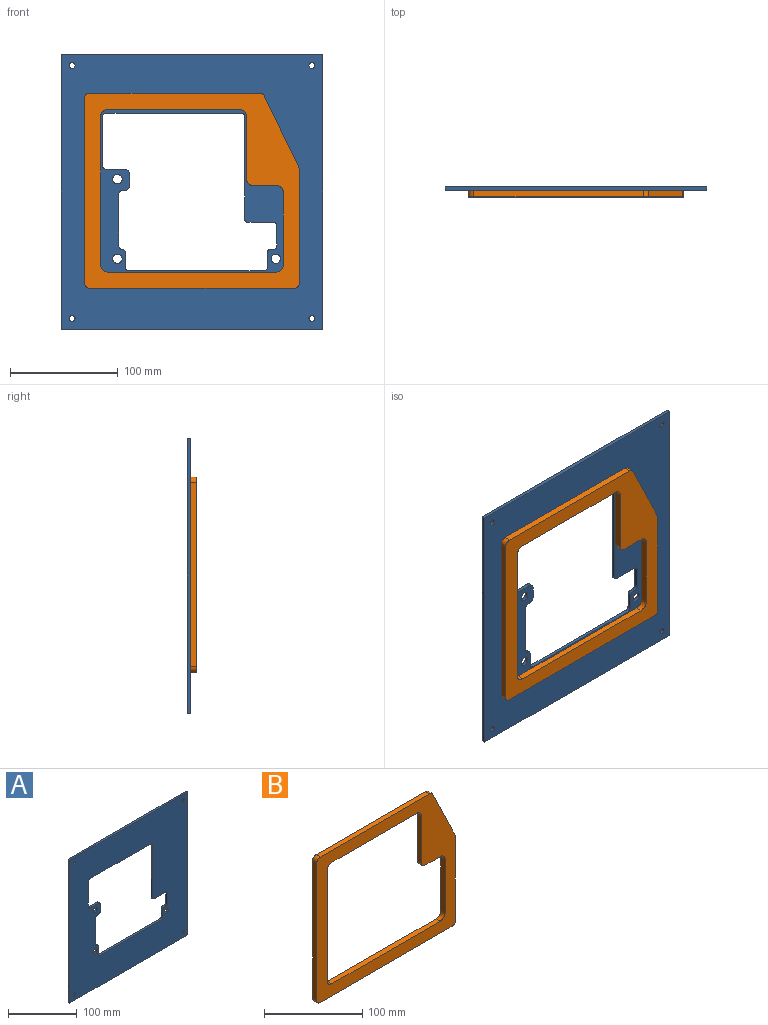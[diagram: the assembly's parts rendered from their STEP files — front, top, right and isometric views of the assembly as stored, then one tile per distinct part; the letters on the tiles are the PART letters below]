
ASSEMBLY  parts=2 mates=1
PART A: 40 faces, bbox 243x3.2x255 mm
  f0: plane 243x3.18mm, normal (0,0,-1), area 771.5mm2, adj f2,f3,f34,f35
  f1: plane 243x3.18mm, normal (0,0,1), area 771.5mm2, adj f2,f3,f34,f35
  f2: plane 255x243mm, normal (0,-1,0), area 42919.9mm2, adj f0,f1,f4,f5,f6,f7,f8,f9
  f3: plane 255x243mm, normal (0,1,0), area 42919.9mm2, adj f0,f1,f4,f5,f6,f7,f8,f9
  f4: plane 95.5x3.18mm, normal (-1,0,0), area 303.2mm2, adj f2,f3,f17,f22
  f5: plane 126x3.18mm, normal (0,0,-1), area 400.1mm2, adj f2,f3,f17,f18
  f6: plane 46x3.18mm, normal (1,0,0), area 146.1mm2, adj f2,f3,f18,f19
  f7: plane 17x3.18mm, normal (0,0,1), area 54mm2, adj f2,f3,f19,f29
  f8: plane 10x3.18mm, normal (1,0,0), area 31.8mm2, adj f2,f3,f29,f30
  f9: plane 3.18x2mm, normal (0,0,-1), area 6.4mm2, adj f2,f3,f23,f30
  f10: plane 48.5x3.18mm, normal (1,0,0), area 154mm2, adj f2,f3,f23,f25
  f11: plane 14x3.18mm, normal (1,0,0), area 44.5mm2, adj f2,f3,f24,f26
  f12: plane 126x3.18mm, normal (0,0,1), area 400.1mm2, adj f2,f3,f20,f26
  f13: plane 14x3.18mm, normal (-1,0,0), area 44.5mm2, adj f2,f3,f20,f21
  f14: plane 3.18x3mm, normal (0,0,1), area 9.5mm2, adj f2,f3,f21,f27
  f15: plane 19x3.18mm, normal (-1,0,0), area 60.3mm2, adj f2,f3,f27,f28
  f16: plane 24x3.18mm, normal (0,0,-1), area 76.2mm2, adj f2,f3,f22,f28
  f17: cylinder r=3mm len=3.18mm, axis (0,-1,0), area 15mm2, adj f2,f3,f4,f5
  f18: cylinder r=3mm len=3.18mm, axis (0,-1,0), area 15mm2, adj f2,f3,f5,f6
  f19: cylinder r=3mm len=3.18mm, axis (0,-1,0), area 15mm2, adj f2,f3,f6,f7
  f20: cylinder r=3mm len=3.18mm, axis (0,-1,0), area 15mm2, adj f2,f3,f12,f13
  f21: cylinder r=3mm len=3.18mm, axis (0,-1,0), area 15mm2, adj f2,f3,f13,f14
  f22: cylinder r=3mm len=3.18mm, axis (0,-1,0), area 15mm2, adj f2,f3,f4,f16
  f23: cylinder r=3mm len=3.18mm, axis (0,-1,0), area 15mm2, adj f2,f3,f9,f10
  f24: cylinder r=3mm len=3.18mm, axis (0,1,0), area 15mm2, adj f2,f3,f11,f25
  f25: cylinder r=3mm len=3.18mm, axis (0,1,0), area 15mm2, adj f2,f3,f10,f24
  f26: cylinder r=3mm len=3.18mm, axis (0,1,0), area 15mm2, adj f2,f3,f11,f12
  f27: cylinder r=3mm len=3.18mm, axis (0,1,0), area 15mm2, adj f2,f3,f14,f15
  f28: cylinder r=3mm len=3.18mm, axis (0,-1,0), area 15mm2, adj f2,f3,f15,f16
  f29: cylinder r=5mm len=5mm, axis (0,-1,0), area 24.9mm2, adj f2,f3,f7,f8
  f30: cylinder r=5mm len=5mm, axis (0,1,0), area 24.9mm2, adj f2,f3,f8,f9
  f31: cylinder r=4.38mm len=8.75mm, axis (0,-1,0), area 87.3mm2, adj f2,f3
  f32: cylinder r=4.38mm len=8.75mm, axis (0,-1,0), area 87.3mm2, adj f2,f3
  f33: cylinder r=4.38mm len=8.75mm, axis (0,-1,0), area 87.3mm2, adj f2,f3
  f34: plane 255x3.18mm, normal (-1,0,0), area 809.6mm2, adj f0,f1,f2,f3
  f35: plane 255x3.18mm, normal (1,0,0), area 809.6mm2, adj f0,f1,f2,f3
  f36: cylinder r=2.75mm len=5.5mm, axis (0,-1,0), area 54.9mm2, adj f2,f3
  f37: cylinder r=2.75mm len=5.5mm, axis (0,-1,0), area 54.9mm2, adj f2,f3
  f38: cylinder r=2.75mm len=5.5mm, axis (0,-1,0), area 54.9mm2, adj f2,f3
  f39: cylinder r=2.75mm len=5.5mm, axis (0,-1,0), area 54.9mm2, adj f2,f3
PART B: 24 faces, bbox 200x6x181.5 mm
  f0: plane 200x181.5mm, normal (0,-1,0), area 11777.1mm2, adj f2,f3,f4,f5,f6,f7,f8,f9
  f1: plane 200x181.5mm, normal (0,1,0), area 11777.1mm2, adj f2,f3,f4,f5,f6,f7,f8,f9
  f2: plane 156x6mm, normal (0,0,1), area 936mm2, adj f0,f1,f8,f12
  f3: plane 66.75x6mm, normal (-1,0,0), area 400.5mm2, adj f0,f1,f8,f9
  f4: plane 22x6mm, normal (0,0,-1), area 132mm2, adj f0,f1,f9,f13
  f5: plane 58.75x6mm, normal (-1,0,0), area 352.5mm2, adj f0,f1,f10,f13
  f6: plane 122x6mm, normal (0,0,-1), area 732mm2, adj f0,f1,f10,f11
  f7: plane 137.5x6mm, normal (1,0,0), area 825mm2, adj f0,f1,f11,f12
  f8: cylinder r=7mm len=7mm, axis (0,-1,0), area 66mm2, adj f0,f1,f2,f3
  f9: cylinder r=7mm len=7mm, axis (0,1,0), area 66mm2, adj f0,f1,f3,f4
  f10: cylinder r=7mm len=7mm, axis (0,-1,0), area 66mm2, adj f0,f1,f5,f6
  f11: cylinder r=7mm len=7mm, axis (0,-1,0), area 66mm2, adj f0,f1,f6,f7
  f12: cylinder r=7mm len=7mm, axis (0,1,0), area 66mm2, adj f0,f1,f2,f7
  f13: cylinder r=5mm len=6mm, axis (0,1,0), area 47.1mm2, adj f0,f1,f4,f5
  f14: plane 190x6mm, normal (0,0,-1), area 1140mm2, adj f0,f1,f19,f23
  f15: plane 171.5x6mm, normal (-1,0,0), area 1029mm2, adj f0,f1,f19,f20
  f16: plane 157.86x6mm, normal (0,0,1), area 947.1mm2, adj f0,f1,f20,f21
  f17: plane 66.89x32.14mm, normal (0.9,0,0.43), area 445.3mm2, adj f0,f1,f21,f22
  f18: plane 104.61x6mm, normal (1,0,0), area 627.7mm2, adj f0,f1,f22,f23
  f19: cylinder r=5mm len=6mm, axis (0,-1,0), area 47.1mm2, adj f0,f1,f14,f15
  f20: cylinder r=5mm len=6mm, axis (0,-1,0), area 47.1mm2, adj f0,f1,f15,f16
  f21: cylinder r=5mm len=6mm, axis (0,1,0), area 33.7mm2, adj f0,f1,f16,f17
  f22: cylinder r=5mm len=6mm, axis (0,1,0), area 13.4mm2, adj f0,f1,f17,f18
  f23: cylinder r=5mm len=6mm, axis (0,-1,0), area 47.1mm2, adj f0,f1,f14,f18
PLACE A t=(-15.55,-0.53,18.64)mm
PLACE B t=(-13.58,-3.7,19.93)mm
MATE planar B.f1 <-> A.f2  axis (0,1,0) through (-91.58,-3.7,95.68)mm
